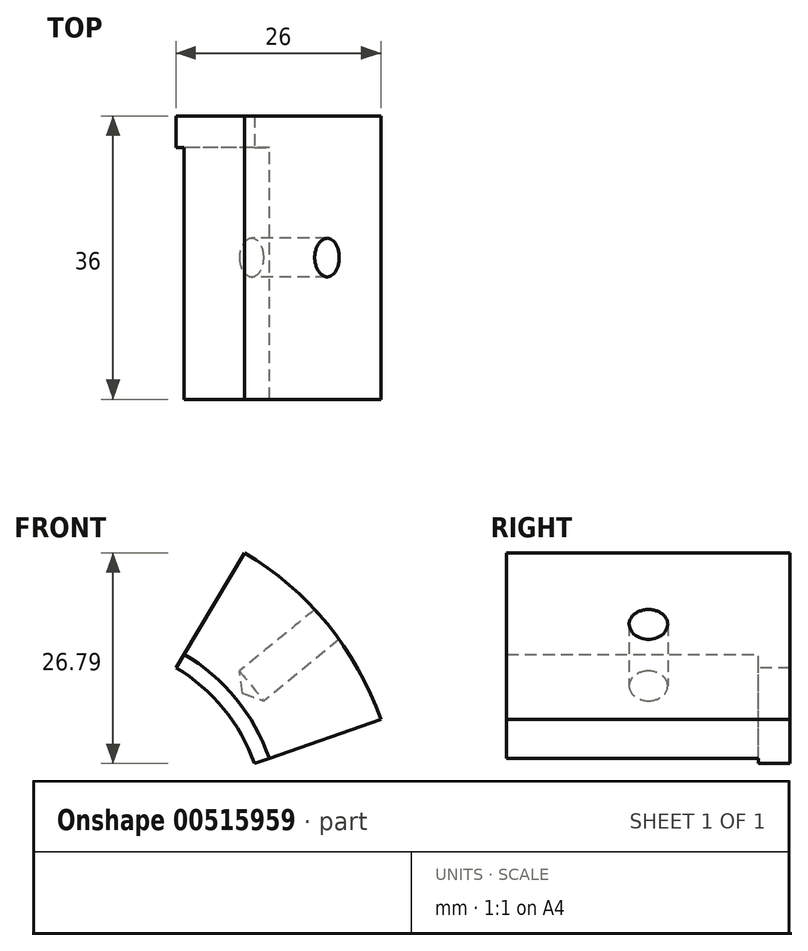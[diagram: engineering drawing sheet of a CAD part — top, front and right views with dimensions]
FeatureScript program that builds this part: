
annotation { "Feature Type Name" : "Feature", "Feature Type Description" : "" }
export const myFeature = defineFeature(function(context is Context, id is Id, definition is map)
    precondition{}
    {
        {
            var Q0;
            Q0=qCreatedBy(makeId("Front.planeOp"),FACE);
            var sketch = newSketch(context, id + "F0", { "sketchPlane" : qUnion([Q0])});
            skArc(sketch, "E0", {"start": v(37.76, 13.18) * mm, "mid": v(30.98, 25.3) * mm, "end": v(20.45, 34.37) * mm});
            skArc(sketch, "E1", {"start": v(23.6, 8.24) * mm, "mid": v(19.36, 15.82) * mm, "end": v(12.78, 21.48) * mm});
            skLineSegment(sketch, "E2", {"start": v(12.78, 21.48) * mm, "end": v(20.45, 34.37) * mm});
            skLineSegment(sketch, "E3", {"start": v(23.6, 8.24) * mm, "end": v(37.76, 13.18) * mm});
            skSolve(sketch);
        }
        {
            var Q0;
            Q0=qCreatedBy(makeId("Front.planeOp"),FACE);
            var sketch = newSketch(context, id + "F1", { "sketchPlane" : qUnion([Q0])});
            skArc(sketch, "E4", {"start": v(21.71, 7.58) * mm, "mid": v(17.81, 14.55) * mm, "end": v(11.76, 19.77) * mm});
            skLineSegment(sketch, "E5", {"start": v(20.5, 34.46) * mm, "end": v(11.76, 19.77) * mm});
            skLineSegment(sketch, "E6", {"start": v(37.76, 13.18) * mm, "end": v(21.71, 7.58) * mm});
            skArc(sketch, "E7", {"start": v(37.76, 13.18) * mm, "mid": v(30.98, 25.3) * mm, "end": v(20.45, 34.37) * mm});
            skSolve(sketch);
        }
        {
            var Q0;
            Q0=makeQuery(id+"F0.imprint","IMPRINT",FACE,{"disambiguationData":[TD([[makeQuery(id+"F0.imprint","IMPRINT",EDGE,{"derivedFrom":sQuery(id+"F0.wireOp",EDGE,"E0")}),1.0]])]});
            extrude(context, id + "F2", {"entities" : qUnion([Q0]), "depth" : 32 * mm, "offsetDistance" : 25 * mm});
        }
        {
            var Q0;
            Q0=qSketchRegion(id+"F1",true);
            var Q1;
            Q1=qSketchRegion(id+"F0",true);
            extrude(context, id + "F3", {"entities" : qUnion([Q0, Q1]), "operationType" : NewBodyOperationType.ADD, "oppositeDirection" : true, "depth" : 4 * mm, "offsetDistance" : 25 * mm});
        }
        {
            var Q0;
            Q0=makeQuery(id+"F2.opExtrude","CAP_VERTEX",VERTEX,{"disambiguationData":[OSD([sQuery(id+"F0.wireOp",EDGE,"E0"),sQuery(id+"F0.wireOp",EDGE,"E3")])],"isStart":false});
            var Q1;
            Q1=makeQuery(id+"F2.opExtrude","CAP_VERTEX",VERTEX,{"disambiguationData":[OSD([sQuery(id+"F0.wireOp",EDGE,"E0"),sQuery(id+"F0.wireOp",EDGE,"E2")])],"isStart":false});
            var Q2;
            Q2=sQuery(id+"F0.wireOp",VERTEX,"E2.end");
            cPlane(context, id + "F4", {"entities" : qUnion([Q0, Q1, Q2]), "cplaneType" : CPlaneType.THREE_POINT, "offset" : 0 * mm, "width" : 150 * mm, "height" : 150 * mm});
        }
        {
            var Q0;
            Q0=qCreatedBy(id+"F4.planeOp",FACE);
            var sketch = newSketch(context, id + "F5", { "sketchPlane" : qUnion([Q0])});
            skCircle(sketch, "E8", {"center": v(-14, 0) * mm, "radius": 2.45 * mm});
            skSolve(sketch);
        }
        {
            var Q0;
            Q0=sQuery(id+"F5.wireOp",VERTEX,"E8.center");
            var Q1;
            Q1=makeQuery(id+"F2.opExtrude","SWEPT_BODY",BODY,{"disambiguationData":[OSD([sQuery(id+"F0.wireOp",EDGE,"E0"),sQuery(id+"F0.wireOp",EDGE,"E1"),sQuery(id+"F0.wireOp",EDGE,"E2"),sQuery(id+"F0.wireOp",EDGE,"E3")])]});
            hole(context, id + "F6", {"style" : HoleStyle.SIMPLE, "endStyle" : HoleEndStyle.BLIND, "oppositeDirection" : true, "holeDiameter" : 4.9 * mm, "holeDepth" : 10 * mm, "isTappedThrough" : true, "tappedDepth" : 12 * mm, "tapClearance" : 3, "locations" : qUnion([Q0]), "scope" : qUnion([Q1])});
        }
        {
            var Q0;
            Q0=sQuery(id+"F5.wireOp",VERTEX,"E8.center");
            var Q1;
            Q1=makeQuery(id+"F2.opExtrude","SWEPT_BODY",BODY,{"disambiguationData":[OSD([sQuery(id+"F0.wireOp",EDGE,"E0"),sQuery(id+"F0.wireOp",EDGE,"E1"),sQuery(id+"F0.wireOp",EDGE,"E2"),sQuery(id+"F0.wireOp",EDGE,"E3")])]});
            hole(context, id + "F7", {"style" : HoleStyle.SIMPLE, "endStyle" : HoleEndStyle.BLIND, "holeDiameter" : 4.9 * mm, "holeDepth" : 10 * mm, "isTappedThrough" : true, "tappedDepth" : 12 * mm, "tapClearance" : 3, "locations" : qUnion([Q0]), "scope" : qUnion([Q1])});
        }
    });
